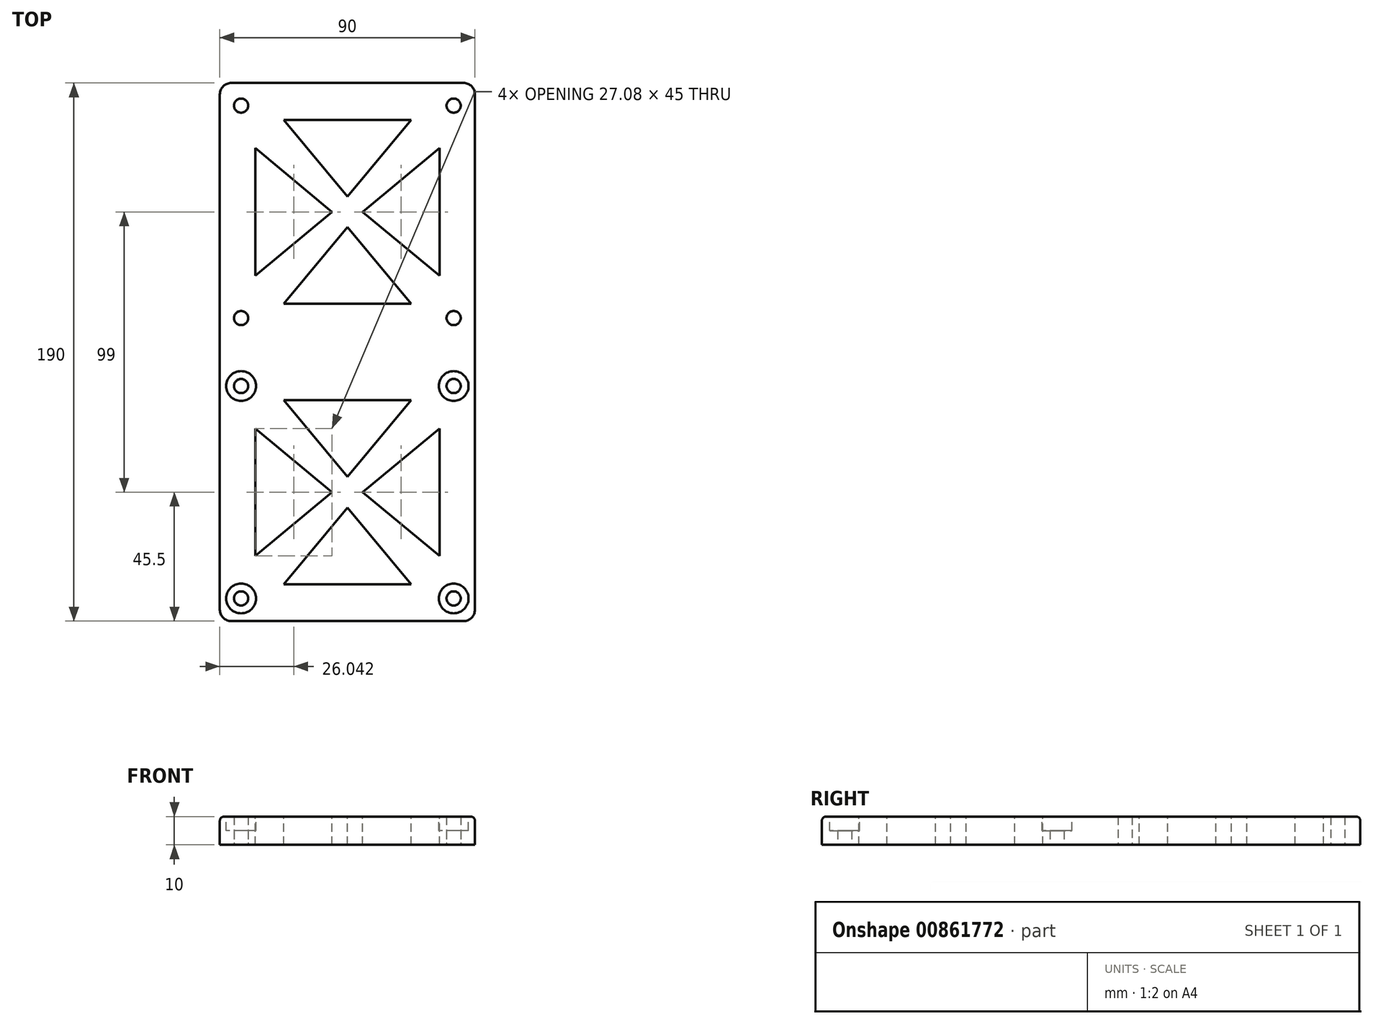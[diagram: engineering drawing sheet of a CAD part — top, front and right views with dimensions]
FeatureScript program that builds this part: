
annotation { "Feature Type Name" : "Feature", "Feature Type Description" : "" }
export const myFeature = defineFeature(function(context is Context, id is Id, definition is map)
    precondition{}
    {
        {
            var Q0;
            Q0=qCreatedBy(makeId("Top.planeOp"),FACE);
            var sketch = newSketch(context, id + "F0", { "sketchPlane" : qUnion([Q0])});
            skLineSegment(sketch, "E0.bottom", {"start": v(45, -95) * mm, "end": v(-45, -95) * mm});
            skLineSegment(sketch, "E0.top", {"start": v(45, 95) * mm, "end": v(-45, 95) * mm});
            skLineSegment(sketch, "E0.left", {"start": v(45, -95) * mm, "end": v(45, 95) * mm});
            skLineSegment(sketch, "E0.right", {"start": v(-45, -95) * mm, "end": v(-45, 95) * mm});
            skPoint(sketch, "E0.middle", {"position": v(0, 0) * mm});
            skLineSegment(sketch, "E1", {"start": v(0, 109.56) * mm, "end": v(0, -105.54) * mm, "construction": true});
            skPoint(sketch, "E1.endSnap0", {"position": v(0, -95) * mm});
            skLineSegment(sketch, "E2", {"start": v(-63.02, 87) * mm, "end": v(69.26, 87) * mm, "construction": true});
            skCircle(sketch, "E3", {"center": v(-37.5, 87) * mm, "radius": 2.5 * mm});
            skLineSegment(sketch, "E4", {"start": v(-37.5, 101.13) * mm, "end": v(-37.5, 34.39) * mm, "construction": true});
            skCircle(sketch, "E5", {"center": v(-37.5, 12) * mm, "radius": 2.5 * mm});
            skCircle(sketch, "E6.MirrorC", {"center": v(37.5, 12) * mm, "radius": 2.5 * mm});
            skCircle(sketch, "E7.MirrorC", {"center": v(37.5, 87) * mm, "radius": 2.5 * mm});
            skCircle(sketch, "E8.MirrorC", {"center": v(-37.5, -12) * mm, "radius": 2.5 * mm});
            skCircle(sketch, "E9.MirrorC", {"center": v(37.5, -12) * mm, "radius": 2.5 * mm});
            skCircle(sketch, "E10.MirrorC", {"center": v(37.5, -87) * mm, "radius": 2.5 * mm});
            skCircle(sketch, "E11.MirrorC", {"center": v(-37.5, -87) * mm, "radius": 2.5 * mm});
            skSolve(sketch);
        }
        {
            var Q0;
            Q0 = qSketchRegion(id + "F0", true);
            extrude(context, id + "F1", {"entities" : qUnion([Q0]), "depth" : 10 * mm, "offsetDistance" : 25 * mm});
        }
        {
            var Q0;
            Q0=makeQuery(id+"F1.opExtrude","CAP_FACE",FACE,{"disambiguationData":[OSD([sQuery(id+"F0.wireOp",EDGE,"E0.bottom"),sQuery(id+"F0.wireOp",EDGE,"E0.top"),sQuery(id+"F0.wireOp",EDGE,"E0.left"),sQuery(id+"F0.wireOp",EDGE,"E0.right"),sQuery(id+"F0.wireOp",EDGE,"E3"),sQuery(id+"F0.wireOp",EDGE,"E5"),sQuery(id+"F0.wireOp",EDGE,"E6.MirrorC"),sQuery(id+"F0.wireOp",EDGE,"E7.MirrorC"),sQuery(id+"F0.wireOp",EDGE,"E8.MirrorC"),sQuery(id+"F0.wireOp",EDGE,"E9.MirrorC"),sQuery(id+"F0.wireOp",EDGE,"E10.MirrorC"),sQuery(id+"F0.wireOp",EDGE,"E11.MirrorC")])],"isStart":false});
            var sketch = newSketch(context, id + "F2", { "sketchPlane" : qUnion([Q0])});
            skCircle(sketch, "E12", {"center": v(-37.5, -12) * mm, "radius": 5.25 * mm});
            skCircle(sketch, "E13.0.1.0", {"center": v(-37.5, -87) * mm, "radius": 5.25 * mm});
            skCircle(sketch, "E13.1.0.0", {"center": v(37.5, -12) * mm, "radius": 5.25 * mm});
            skCircle(sketch, "E13.1.1.0", {"center": v(37.5, -87) * mm, "radius": 5.25 * mm});
            skLineSegment(sketch, "E13.direction1", {"start": v(-37.5, -12) * mm, "end": v(37.5, -12) * mm, "construction": true});
            skLineSegment(sketch, "E13.direction2", {"start": v(-37.5, -12) * mm, "end": v(-37.5, -87) * mm, "construction": true});
            skSolve(sketch);
        }
        {
            var Q0;
            Q0 = qSketchRegion(id + "F2", true);
            extrude(context, id + "F3", {"entities" : qUnion([Q0]), "operationType" : NewBodyOperationType.REMOVE, "oppositeDirection" : true, "depth" : 5 * mm, "offsetDistance" : 25 * mm});
        }
        {
            var Q0;
            Q0=makeQuery(id+"F1.opExtrude","CAP_EDGE",EDGE,{"disambiguationData":[OSD([sQuery(id+"F0.wireOp",EDGE,"E0.right")])],"isStart":false});
            var Q1;
            Q1=makeQuery(id+"F1.opExtrude","CAP_EDGE",EDGE,{"disambiguationData":[OSD([sQuery(id+"F0.wireOp",EDGE,"E0.top")])],"isStart":false});
            var Q2;
            Q2=makeQuery(id+"F1.opExtrude","CAP_EDGE",EDGE,{"disambiguationData":[OSD([sQuery(id+"F0.wireOp",EDGE,"E0.left")])],"isStart":false});
            var Q3;
            Q3=makeQuery(id+"F1.opExtrude","CAP_EDGE",EDGE,{"disambiguationData":[OSD([sQuery(id+"F0.wireOp",EDGE,"E0.bottom")])],"isStart":false});
            var Q4;
            Q4=makeQuery(id+"F3.boolean.opBoolean","COPY",EDGE,{"derivedFrom":makeQuery(id+"F3.opExtrude","CAP_EDGE",EDGE,{"disambiguationData":[OSD([sQuery(id+"F2.wireOp",EDGE,"E13.0.1.0")])],"isStart":true})});
            var Q5;
            Q5=makeQuery(id+"F3.boolean.opBoolean","COPY",EDGE,{"derivedFrom":makeQuery(id+"F3.opExtrude","CAP_EDGE",EDGE,{"disambiguationData":[OSD([sQuery(id+"F2.wireOp",EDGE,"E12")])],"isStart":true})});
            var Q6;
            Q6=makeQuery(id+"F3.boolean.opBoolean","COPY",EDGE,{"derivedFrom":makeQuery(id+"F3.opExtrude","CAP_EDGE",EDGE,{"disambiguationData":[OSD([sQuery(id+"F2.wireOp",EDGE,"E13.1.0.0")])],"isStart":true})});
            var Q7;
            Q7=makeQuery(id+"F3.boolean.opBoolean","COPY",EDGE,{"derivedFrom":makeQuery(id+"F3.opExtrude","CAP_EDGE",EDGE,{"disambiguationData":[OSD([sQuery(id+"F2.wireOp",EDGE,"E13.1.1.0")])],"isStart":true})});
            fillet(context, id + "F4", {"entities" : qUnion([Q0, Q1, Q2, Q3, Q4, Q5, Q6, Q7]), "radius" : 1.5 * mm, "tangentPropagation" : true, "allowEdgeOverflow" : false});
        }
        {
            var Q0;
            Q0=makeQuery(id+"F1.opExtrude","SWEPT_EDGE",EDGE,{"disambiguationData":[OSD([sQuery(id+"F0.wireOp",EDGE,"E0.bottom"),sQuery(id+"F0.wireOp",EDGE,"E0.right")])]});
            var Q1;
            Q1=makeQuery(id+"F1.opExtrude","SWEPT_EDGE",EDGE,{"disambiguationData":[OSD([sQuery(id+"F0.wireOp",EDGE,"E0.bottom"),sQuery(id+"F0.wireOp",EDGE,"E0.left")])]});
            var Q2;
            Q2=makeQuery(id+"F1.opExtrude","SWEPT_EDGE",EDGE,{"disambiguationData":[OSD([sQuery(id+"F0.wireOp",EDGE,"E0.top"),sQuery(id+"F0.wireOp",EDGE,"E0.left")])]});
            var Q3;
            Q3=makeQuery(id+"F1.opExtrude","SWEPT_EDGE",EDGE,{"disambiguationData":[OSD([sQuery(id+"F0.wireOp",EDGE,"E0.top"),sQuery(id+"F0.wireOp",EDGE,"E0.right")])]});
            fillet(context, id + "F5", {"entities" : qUnion([Q0, Q1, Q2, Q3]), "radius" : 4 * mm, "tangentPropagation" : true, "allowEdgeOverflow" : false});
        }
        {
            var Q0;
            Q0=makeQuery(id+"F4.opFillet","SPLIT",FACE,{"disambiguationData":[OD(2.0)],"derivedFrom":makeQuery(id+"F1.opExtrude","CAP_FACE",FACE,{"disambiguationData":[OSD([sQuery(id+"F0.wireOp",EDGE,"E0.bottom"),sQuery(id+"F0.wireOp",EDGE,"E0.top"),sQuery(id+"F0.wireOp",EDGE,"E0.left"),sQuery(id+"F0.wireOp",EDGE,"E0.right"),sQuery(id+"F0.wireOp",EDGE,"E3"),sQuery(id+"F0.wireOp",EDGE,"E5"),sQuery(id+"F0.wireOp",EDGE,"E6.MirrorC"),sQuery(id+"F0.wireOp",EDGE,"E7.MirrorC"),sQuery(id+"F0.wireOp",EDGE,"E8.MirrorC"),sQuery(id+"F0.wireOp",EDGE,"E9.MirrorC"),sQuery(id+"F0.wireOp",EDGE,"E10.MirrorC"),sQuery(id+"F0.wireOp",EDGE,"E11.MirrorC")])],"isStart":false})});
            var sketch = newSketch(context, id + "F6", { "sketchPlane" : qUnion([Q0])});
            skLineSegment(sketch, "E14", {"start": v(-37.5, -12) * mm, "end": v(-37.5, -87) * mm, "construction": true});
            skLineSegment(sketch, "E15", {"start": v(-32.5, -27) * mm, "end": v(-32.5, -72) * mm});
            skLineSegment(sketch, "E16", {"start": v(-37.5, -12) * mm, "end": v(37.5, -12) * mm, "construction": true});
            skLineSegment(sketch, "E17", {"start": v(-32.5, -49.5) * mm, "end": v(17.5, -49.5) * mm, "construction": true});
            skLineSegment(sketch, "E18", {"start": v(-32.5, -27) * mm, "end": v(-5.42, -49.5) * mm});
            skLineSegment(sketch, "E19", {"start": v(-5.42, -49.5) * mm, "end": v(-32.5, -72) * mm});
            skLineSegment(sketch, "E20.1.0", {"start": v(22.5, -17) * mm, "end": v(0, -44.08) * mm});
            skLineSegment(sketch, "E20.1.1", {"start": v(22.5, -17) * mm, "end": v(-22.5, -17) * mm});
            skLineSegment(sketch, "E20.1.2", {"start": v(0, -44.08) * mm, "end": v(-22.5, -17) * mm});
            skLineSegment(sketch, "E20.2.0", {"start": v(32.5, -72) * mm, "end": v(5.42, -49.5) * mm});
            skLineSegment(sketch, "E20.2.1", {"start": v(32.5, -72) * mm, "end": v(32.5, -27) * mm});
            skLineSegment(sketch, "E20.2.2", {"start": v(5.42, -49.5) * mm, "end": v(32.5, -27) * mm});
            skLineSegment(sketch, "E20.3.0", {"start": v(-22.5, -82) * mm, "end": v(0, -54.92) * mm});
            skLineSegment(sketch, "E20.3.1", {"start": v(-22.5, -82) * mm, "end": v(22.5, -82) * mm});
            skLineSegment(sketch, "E20.3.2", {"start": v(0, -54.92) * mm, "end": v(22.5, -82) * mm});
            skPoint(sketch, "E20.center", {"position": v(0, -49.5) * mm});
            skLineSegment(sketch, "E21.MirrorCS", {"start": v(-32.5, 27) * mm, "end": v(-32.5, 72) * mm});
            skLineSegment(sketch, "E22.MirrorCS", {"start": v(-32.5, 27) * mm, "end": v(-5.42, 49.5) * mm});
            skLineSegment(sketch, "E23.MirrorCS", {"start": v(-5.42, 49.5) * mm, "end": v(-32.5, 72) * mm});
            skLineSegment(sketch, "E24.MirrorCS", {"start": v(-22.5, 82) * mm, "end": v(0, 54.92) * mm});
            skLineSegment(sketch, "E25.MirrorCS", {"start": v(-22.5, 82) * mm, "end": v(22.5, 82) * mm});
            skLineSegment(sketch, "E26.MirrorCS", {"start": v(0, 54.92) * mm, "end": v(22.5, 82) * mm});
            skLineSegment(sketch, "E27.MirrorCS", {"start": v(32.5, 72) * mm, "end": v(5.42, 49.5) * mm});
            skLineSegment(sketch, "E28.MirrorCS", {"start": v(32.5, 72) * mm, "end": v(32.5, 27) * mm});
            skLineSegment(sketch, "E29.MirrorCS", {"start": v(5.42, 49.5) * mm, "end": v(32.5, 27) * mm});
            skLineSegment(sketch, "E30.MirrorCS", {"start": v(22.5, 17) * mm, "end": v(0, 44.08) * mm});
            skLineSegment(sketch, "E31.MirrorCS", {"start": v(0, 44.08) * mm, "end": v(-22.5, 17) * mm});
            skLineSegment(sketch, "E32.MirrorCS", {"start": v(22.5, 17) * mm, "end": v(-22.5, 17) * mm});
            skSolve(sketch);
        }
        {
            var Q0;
            Q0=makeQuery(id+"F6.imprint","IMPRINT",FACE,{"disambiguationData":[TD([[makeQuery(id+"F6.imprint","IMPRINT",EDGE,{"derivedFrom":sQuery(id+"F6.wireOp",EDGE,"E20.1.0")}),-1.0]])]});
            var Q1;
            Q1=makeQuery(id+"F6.imprint","IMPRINT",FACE,{"disambiguationData":[TD([[makeQuery(id+"F6.imprint","IMPRINT",EDGE,{"derivedFrom":sQuery(id+"F6.wireOp",EDGE,"E15")}),1.0]])]});
            var Q2;
            Q2=makeQuery(id+"F6.imprint","IMPRINT",FACE,{"disambiguationData":[TD([[makeQuery(id+"F6.imprint","IMPRINT",EDGE,{"derivedFrom":sQuery(id+"F6.wireOp",EDGE,"E20.3.0")}),-1.0]])]});
            var Q3;
            Q3=makeQuery(id+"F6.imprint","IMPRINT",FACE,{"disambiguationData":[TD([[makeQuery(id+"F6.imprint","IMPRINT",EDGE,{"derivedFrom":sQuery(id+"F6.wireOp",EDGE,"E20.2.0")}),-1.0]])]});
            var Q4;
            Q4=makeQuery(id+"F6.imprint","IMPRINT",FACE,{"disambiguationData":[TD([[makeQuery(id+"F6.imprint","IMPRINT",EDGE,{"derivedFrom":sQuery(id+"F6.wireOp",EDGE,"E30.MirrorCS")}),1.0]])]});
            var Q5;
            Q5=makeQuery(id+"F6.imprint","IMPRINT",FACE,{"disambiguationData":[TD([[makeQuery(id+"F6.imprint","IMPRINT",EDGE,{"derivedFrom":sQuery(id+"F6.wireOp",EDGE,"E27.MirrorCS")}),1.0]])]});
            var Q6;
            Q6=makeQuery(id+"F6.imprint","IMPRINT",FACE,{"disambiguationData":[TD([[makeQuery(id+"F6.imprint","IMPRINT",EDGE,{"derivedFrom":sQuery(id+"F6.wireOp",EDGE,"E24.MirrorCS")}),1.0]])]});
            var Q7;
            Q7=makeQuery(id+"F6.imprint","IMPRINT",FACE,{"disambiguationData":[TD([[makeQuery(id+"F6.imprint","IMPRINT",EDGE,{"derivedFrom":sQuery(id+"F6.wireOp",EDGE,"E21.MirrorCS")}),-1.0]])]});
            var Q8;
            Q8=makeQuery(id+"F1.opExtrude","CAP_FACE",FACE,{"disambiguationData":[OSD([sQuery(id+"F0.wireOp",EDGE,"E0.bottom"),sQuery(id+"F0.wireOp",EDGE,"E0.top"),sQuery(id+"F0.wireOp",EDGE,"E0.left"),sQuery(id+"F0.wireOp",EDGE,"E0.right"),sQuery(id+"F0.wireOp",EDGE,"E3"),sQuery(id+"F0.wireOp",EDGE,"E5"),sQuery(id+"F0.wireOp",EDGE,"E6.MirrorC"),sQuery(id+"F0.wireOp",EDGE,"E7.MirrorC"),sQuery(id+"F0.wireOp",EDGE,"E8.MirrorC"),sQuery(id+"F0.wireOp",EDGE,"E9.MirrorC"),sQuery(id+"F0.wireOp",EDGE,"E10.MirrorC"),sQuery(id+"F0.wireOp",EDGE,"E11.MirrorC")])],"isStart":true});
            extrude(context, id + "F7", {"entities" : qUnion([Q0, Q1, Q2, Q3, Q4, Q5, Q6, Q7]), "operationType" : NewBodyOperationType.REMOVE, "endBound" : BoundingType.UP_TO_SURFACE, "oppositeDirection" : true, "depth" : 25 * mm, "endBoundEntityFace" : qUnion([Q8]), "offsetDistance" : 25 * mm});
        }
    });
